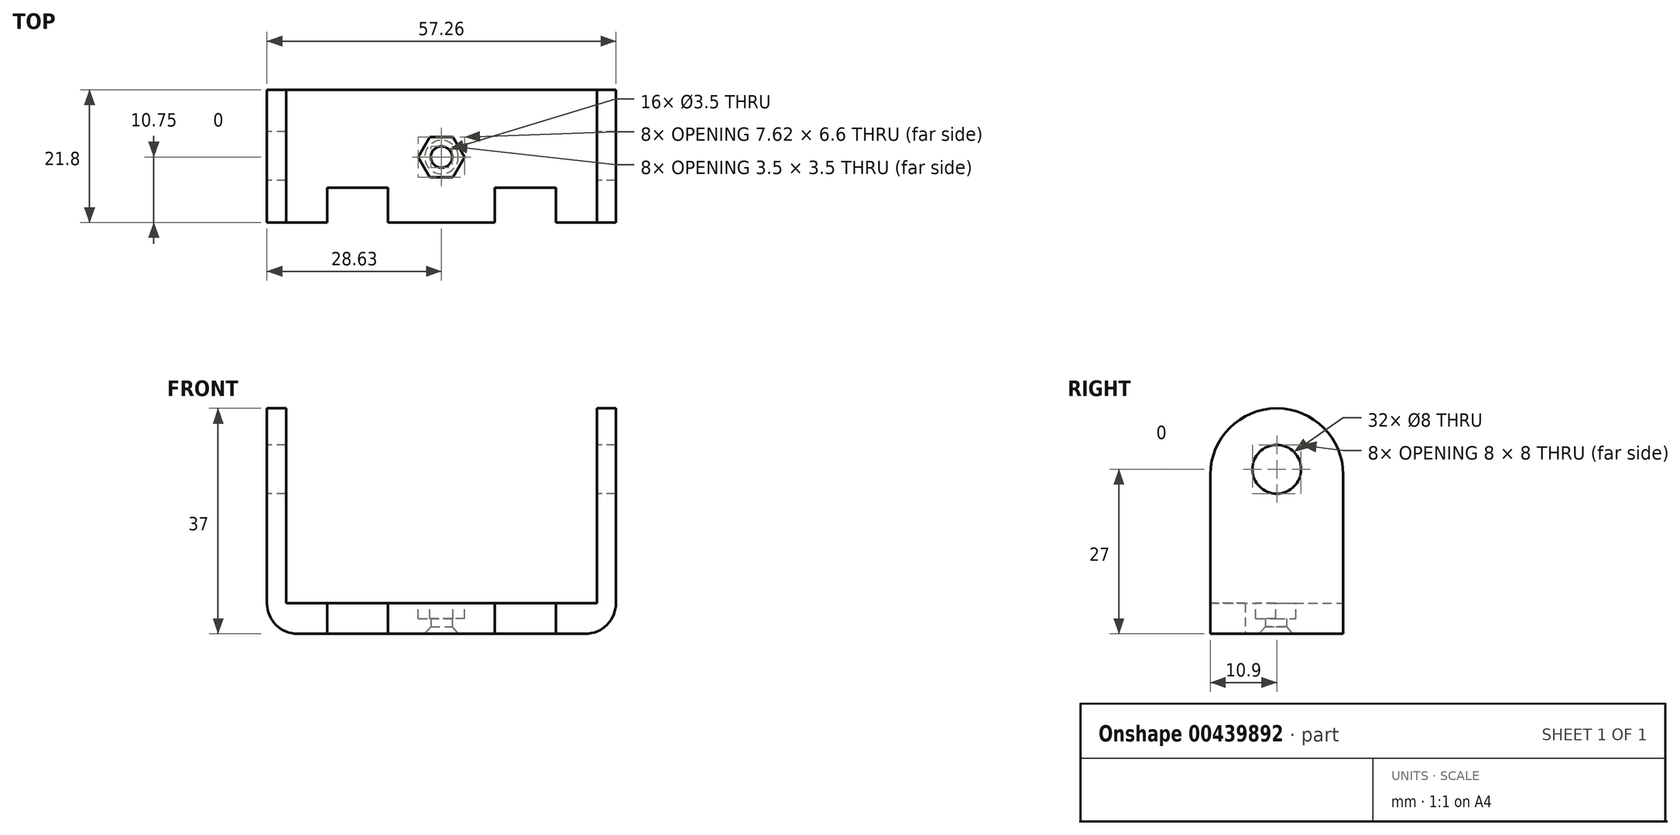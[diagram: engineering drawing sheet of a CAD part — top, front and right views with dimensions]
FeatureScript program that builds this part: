
annotation { "Feature Type Name" : "Feature", "Feature Type Description" : "" }
export const myFeature = defineFeature(function(context is Context, id is Id, definition is map)
    precondition{}
    {
        {
            var Q0;
            Q0=qCreatedBy(makeId("Front.planeOp"),FACE);
            var sketch = newSketch(context, id + "F0", { "sketchPlane" : qUnion([Q0])});
            skLineSegment(sketch, "E0.bottom", {"start": v(-28.62, 37) * mm, "end": v(-25.5, 37) * mm});
            skLineSegment(sketch, "E0.top", {"start": v(-25.5, 5) * mm, "end": v(25.5, 5) * mm});
            skLineSegment(sketch, "E0.left", {"start": v(-25.5, 37) * mm, "end": v(-25.5, 5) * mm});
            skLineSegment(sketch, "E0.right", {"start": v(25.5, 37) * mm, "end": v(25.5, 5) * mm});
            skLineSegment(sketch, "E1", {"start": v(-28.62, 37) * mm, "end": v(-28.62, 0) * mm});
            skLineSegment(sketch, "E2", {"start": v(28.62, 37) * mm, "end": v(28.62, 0) * mm});
            skLineSegment(sketch, "E3.trimOffspring", {"start": v(25.5, 37) * mm, "end": v(28.62, 37) * mm});
            skLineSegment(sketch, "E4", {"start": v(-28.62, 0) * mm, "end": v(28.62, 0) * mm});
            skSolve(sketch);
        }
        {
            var Q0;
            Q0=makeQuery(id+"F0.imprint","IMPRINT",FACE,{"disambiguationData":[TD([[makeQuery(id+"F0.imprint","IMPRINT",EDGE,{"derivedFrom":sQuery(id+"F0.wireOp",EDGE,"E0.bottom")}),-1.0]])]});
            extrude(context, id + "F1", {"entities" : qUnion([Q0]), "depth" : 21.8 * mm, "offsetDistance" : 25 * mm});
        }
        {
            var Q0;
            Q0=makeQuery(id+"F1.opExtrude","SWEPT_FACE",FACE,{"disambiguationData":[OSD([sQuery(id+"F0.wireOp",EDGE,"E1")])]});
            var sketch = newSketch(context, id + "F2", { "sketchPlane" : qUnion([Q0])});
            skCircle(sketch, "E5", {"center": v(10.9, 27) * mm, "radius": 4 * mm});
            skLineSegment(sketch, "E6", {"start": v(10.9, 27) * mm, "end": v(10.9, 0) * mm, "construction": true});
            skSolve(sketch);
        }
        {
            var Q0;
            Q0=makeQuery(id+"F2.imprint","IMPRINT",FACE,{"disambiguationData":[TD([[makeQuery(id+"F2.imprint","IMPRINT",EDGE,{"derivedFrom":sQuery(id+"F2.wireOp",EDGE,"E5")}),1.0]])]});
            extrude(context, id + "F3", {"entities" : qUnion([Q0]), "operationType" : NewBodyOperationType.REMOVE, "oppositeDirection" : true, "depth" : 69.8 * mm, "offsetDistance" : 25 * mm});
        }
        {
            var Q0;
            Q0=makeQuery(id+"F1.opExtrude","CAP_EDGE",EDGE,{"disambiguationData":[OSD([sQuery(id+"F0.wireOp",EDGE,"E0.bottom")])],"isStart":false});
            var Q1;
            Q1=makeQuery(id+"F1.opExtrude","CAP_EDGE",EDGE,{"disambiguationData":[OSD([sQuery(id+"F0.wireOp",EDGE,"E0.bottom")])],"isStart":true});
            var Q2;
            Q2=makeQuery(id+"F1.opExtrude","CAP_EDGE",EDGE,{"disambiguationData":[OSD([sQuery(id+"F0.wireOp",EDGE,"E3.trimOffspring")])],"isStart":true});
            var Q3;
            Q3=makeQuery(id+"F1.opExtrude","CAP_EDGE",EDGE,{"disambiguationData":[OSD([sQuery(id+"F0.wireOp",EDGE,"E3.trimOffspring")])],"isStart":false});
            fillet(context, id + "F4", {"entities" : qUnion([Q0, Q1, Q2, Q3]), "radius" : (21.8 / 2) * mm, "tangentPropagation" : true, "allowEdgeOverflow" : false});
        }
        {
            var Q0;
            Q0=makeQuery(id+"F1.opExtrude","SWEPT_FACE",FACE,{"disambiguationData":[OSD([sQuery(id+"F0.wireOp",EDGE,"E4")])]});
            var sketch = newSketch(context, id + "F5", { "sketchPlane" : qUnion([Q0])});
            skLineSegment(sketch, "E7.bottom", {"start": v(-18.75, 22.8) * mm, "end": v(-8.75, 22.8) * mm});
            skLineSegment(sketch, "E7.top", {"start": v(-18.75, 16.05) * mm, "end": v(-8.75, 16.05) * mm});
            skLineSegment(sketch, "E7.left", {"start": v(-18.75, 22.8) * mm, "end": v(-18.75, 16.05) * mm});
            skLineSegment(sketch, "E7.right", {"start": v(-8.75, 22.8) * mm, "end": v(-8.75, 16.05) * mm});
            skLineSegment(sketch, "E8.MirrorCS", {"start": v(18.75, 16.05) * mm, "end": v(8.75, 16.05) * mm});
            skLineSegment(sketch, "E9.MirrorCS", {"start": v(18.75, 22.8) * mm, "end": v(8.75, 22.8) * mm});
            skLineSegment(sketch, "E10.MirrorCS", {"start": v(8.75, 22.8) * mm, "end": v(8.75, 16.05) * mm});
            skLineSegment(sketch, "E11.MirrorCS", {"start": v(18.75, 22.8) * mm, "end": v(18.75, 16.05) * mm});
            skLineSegment(sketch, "E12", {"start": v(0, 0) * mm, "end": v(0, 21.8) * mm, "construction": true});
            skLineSegment(sketch, "E13", {"start": v(0, 11.05) * mm, "end": v(11.64, 11.05) * mm, "construction": true});
            skSolve(sketch);
        }
        {
            var Q0;
            {var subQ0=sQuery(id+"F5.wireOp",EDGE,"E7.top");Q0=makeQuery(id+"F5.imprint","IMPRINT",FACE,{"disambiguationData":[TD([[makeQuery(id+"F5.imprint","IMPRINT",EDGE,{"derivedFrom":subQ0}),1.0]])]});}
            var Q1;
            {var subQ0=sQuery(id+"F5.wireOp",EDGE,"E7.bottom");Q1=makeQuery(id+"F5.imprint","IMPRINT",FACE,{"disambiguationData":[TD([[makeQuery(id+"F5.imprint","IMPRINT",EDGE,{"derivedFrom":subQ0}),-1.0]])]});}
            var Q2;
            {var subQ0=sQuery(id+"F5.wireOp",EDGE,"E9.MirrorCS");Q2=makeQuery(id+"F5.imprint","IMPRINT",FACE,{"disambiguationData":[TD([[makeQuery(id+"F5.imprint","IMPRINT",EDGE,{"derivedFrom":subQ0}),1.0]])]});}
            var Q3;
            {var subQ0=sQuery(id+"F5.wireOp",EDGE,"E8.MirrorCS");Q3=makeQuery(id+"F5.imprint","IMPRINT",FACE,{"disambiguationData":[TD([[makeQuery(id+"F5.imprint","IMPRINT",EDGE,{"derivedFrom":subQ0}),-1.0]])]});}
            extrude(context, id + "F6", {"entities" : qUnion([Q0, Q1, Q2, Q3]), "operationType" : NewBodyOperationType.REMOVE, "oppositeDirection" : true, "depth" : 25 * mm, "offsetDistance" : 25 * mm});
        }
        {
            var Q0;
            Q0=sQuery(id+"F5.wireOp",VERTEX,"E13.start");
            var Q1;
            Q1=makeQuery(id+"F1.opExtrude","SWEPT_BODY",BODY,{"disambiguationData":[OSD([sQuery(id+"F0.wireOp",EDGE,"E0.bottom"),sQuery(id+"F0.wireOp",EDGE,"E0.top"),sQuery(id+"F0.wireOp",EDGE,"E0.left"),sQuery(id+"F0.wireOp",EDGE,"E0.right"),sQuery(id+"F0.wireOp",EDGE,"E1"),sQuery(id+"F0.wireOp",EDGE,"E2"),sQuery(id+"F0.wireOp",EDGE,"E3.trimOffspring"),sQuery(id+"F0.wireOp",EDGE,"E4")])]});
            hole(context, id + "F7", {"style" : HoleStyle.C_SINK, "endStyle" : HoleEndStyle.BLIND, "holeDiameter" : 3.5 * mm, "cSinkDiameter" : 5.5 * mm, "cSinkAngle" : 82 * degree, "majorDiameter" : 5 * mm, "holeDepth" : 10 * mm, "isTappedThrough" : true, "tappedDepth" : 12 * mm, "tapClearance" : 3, "startFromSketch" : true, "locations" : qUnion([Q0]), "scope" : qUnion([Q1])});
        }
        {
            var Q0;
            Q0=makeQuery(id+"F1.opExtrude","SWEPT_FACE",FACE,{"disambiguationData":[OSD([sQuery(id+"F0.wireOp",EDGE,"E0.top")])]});
            var sketch = newSketch(context, id + "F8", { "sketchPlane" : qUnion([Q0])});
            skCircle(sketch, "E14.cCircle", {"center": v(0, -11.05) * mm, "radius": 3.3 * mm, "construction": true});
            skLineSegment(sketch, "E14.0", {"start": v(-1.9, -7.75) * mm, "end": v(1.9, -7.75) * mm});
            skLineSegment(sketch, "E14.1", {"start": v(1.9, -7.75) * mm, "end": v(3.81, -11.05) * mm});
            skLineSegment(sketch, "E14.2", {"start": v(3.81, -11.05) * mm, "end": v(1.9, -14.35) * mm});
            skLineSegment(sketch, "E14.3", {"start": v(1.9, -14.35) * mm, "end": v(-1.9, -14.35) * mm});
            skLineSegment(sketch, "E14.4", {"start": v(-1.9, -14.35) * mm, "end": v(-3.81, -11.05) * mm});
            skLineSegment(sketch, "E14.5", {"start": v(-3.81, -11.05) * mm, "end": v(-1.9, -7.75) * mm});
            skPoint(sketch, "E14.0.midPoint", {"position": v(0, -7.75) * mm});
            skSolve(sketch);
        }
        {
            var Q0;
            Q0=makeQuery(id+"F8.imprint","IMPRINT",FACE,{"disambiguationData":[TD([[makeQuery(id+"F8.imprint","IMPRINT",EDGE,{"derivedFrom":sQuery(id+"F8.wireOp",EDGE,"E14.0")}),-1.0]])]});
            extrude(context, id + "F9", {"entities" : qUnion([Q0]), "operationType" : NewBodyOperationType.REMOVE, "oppositeDirection" : true, "depth" : 2.5 * mm, "offsetDistance" : 25 * mm});
        }
        {
            var Q0;
            Q0=makeQuery(id+"F1.opExtrude","SWEPT_EDGE",EDGE,{"disambiguationData":[OSD([sQuery(id+"F0.wireOp",EDGE,"E1"),sQuery(id+"F0.wireOp",EDGE,"E4")])]});
            var Q1;
            Q1=makeQuery(id+"F1.opExtrude","SWEPT_EDGE",EDGE,{"disambiguationData":[OSD([sQuery(id+"F0.wireOp",EDGE,"E2"),sQuery(id+"F0.wireOp",EDGE,"E4")])]});
            fillet(context, id + "F10", {"entities" : qUnion([Q0, Q1]), "radius" : 5 * mm, "tangentPropagation" : true, "allowEdgeOverflow" : false});
        }
    });
